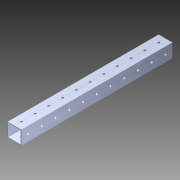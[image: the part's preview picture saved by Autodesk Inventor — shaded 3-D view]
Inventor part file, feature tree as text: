
AUTODESK INVENTOR PART (.ipt)
format: ipt  version: 2014 (Build 180170000, 170)  size: 1,326,592 bytes
history: native  units: in
note: dims shown in document units (in); Inventor stores cm internally (conversion verified against a paired STEP export)
features: extrude x2, sketch x2, pattern_circular x1, other x1, mirror x1, imported_body x1
ambient origin geometry x8: Origin, YZ Plane, XZ Plane, XY Plane, X Axis, Y Axis, Z Axis, Center Point
bodies: Body1 (feature_tree)
feature tree (8):
  pattern_circular  "CirPattern2"
  other  "1x1 tube1"
  extrude  "Extrusion1"  Depth=3.0in TaperAngle=0.0deg
  mirror  "Mirror1"
  extrude  "Extrusion2"  [1 undecoded]
  imported_body  "Base1"
  sketch  "Sketch1"  dims[d0=52.0in d1=0.0in d2=3.0in d3=0.0in]
  sketch  "Sketch4"
note: 1 required parameter value undecoded (feature->parameter linkage not recoverable at this tier; creation-order binding heuristic only, values carry confidence <= 0.55)
